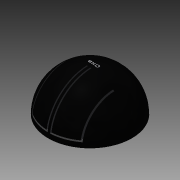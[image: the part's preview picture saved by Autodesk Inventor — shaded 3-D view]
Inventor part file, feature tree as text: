
AUTODESK INVENTOR PART (.ipt)
format: ipt  version: 2015 (Build 190159000, 159)  size: 313,856 bytes
history: native  units: in
note: dims shown in document units (in); Inventor stores cm internally (conversion verified against a paired STEP export)
features: sketch x4, plane x2, extrude x2, revolve x1, shell x1
ambient origin geometry x8: Origin, YZ Plane, XZ Plane, XY Plane, X Axis, Y Axis, Z Axis, Center Point
bodies: Solid1 (feature_tree)
feature tree (10):
  revolve  "Revolution1"  Angle=90.0deg
  shell  "Shell1"  Thickness=0.125in
  plane  "Work Plane1"
  extrude  "Extrusion1"  Depth=1.0in
  plane  "Work Plane2"
  extrude  "Extrusion2"  Depth=1.25in
  sketch  "Sketch4"  dims[d7=1.25in d8=0.05in d9=0.05in d10=0.05in d11=0.05in d12=1.7in d13=0.0in d14=0.03in d15=0.0in d16=0.125in]
  sketch  "Sketch1"  dims[d0=3.5in d1=90.0deg d2=0.125in]
  sketch  "Sketch2"  dims[d3=1.0in d4=1.0in]
  sketch  "Sketch3"  dims[d5=0.1in d6=1.25in]
